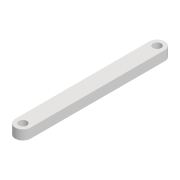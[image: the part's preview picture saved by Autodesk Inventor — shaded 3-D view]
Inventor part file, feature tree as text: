
AUTODESK INVENTOR PART (.ipt)
format: ipt  version: 2022 (Build 260153000, 153)  size: 87,552 bytes
history: native  units: mm
features: extrude x1, sketch x1
ambient origin geometry x8: Origin, YZ Plane, XZ Plane, XY Plane, X Axis, Y Axis, Z Axis, Center Point
bodies: Solid1 (feature_tree)
feature tree (2):
  extrude  "Extrusion1"  Depth=8.0mm
  sketch  "Sketch1"  dims[d0=68.0mm d1=8.0mm d2=4.2mm d3=4.2mm d4=5.0mm d5=0.0mm]
